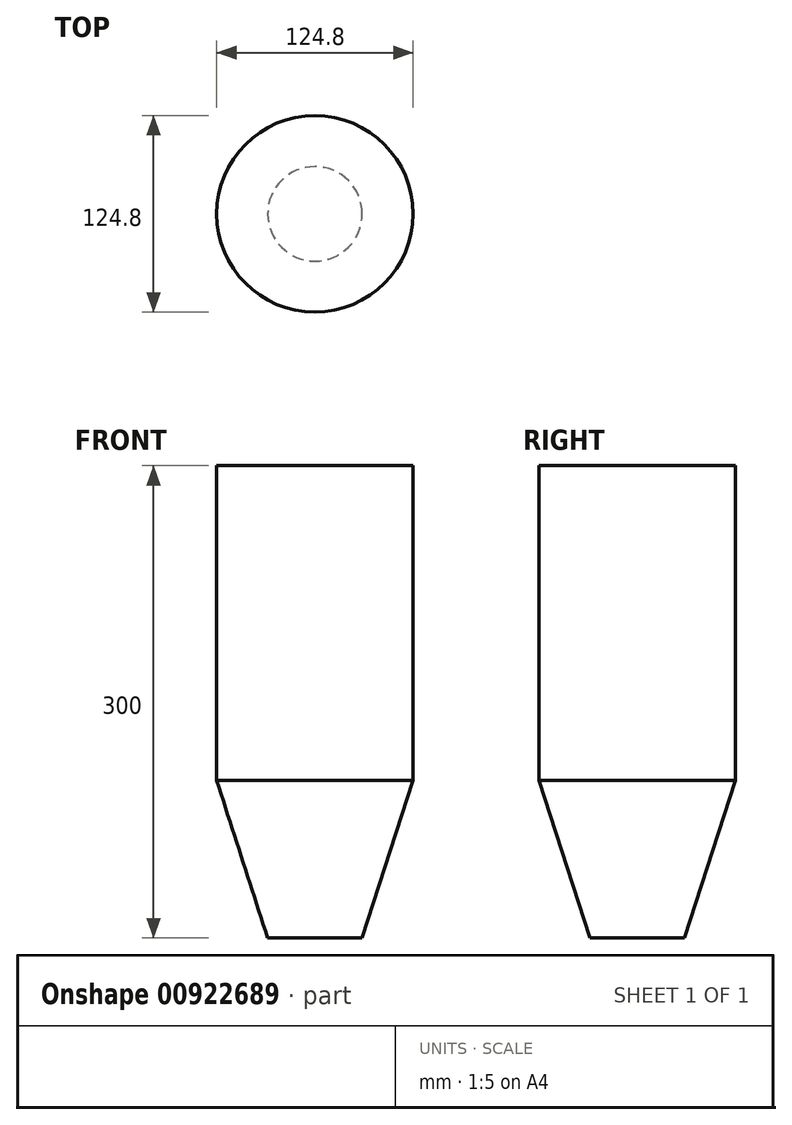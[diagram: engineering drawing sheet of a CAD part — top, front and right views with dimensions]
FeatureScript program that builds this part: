
annotation { "Feature Type Name" : "Feature", "Feature Type Description" : "" }
export const myFeature = defineFeature(function(context is Context, id is Id, definition is map)
    precondition{}
    {
        {
            var Q0;
            Q0=qCreatedBy(makeId("Front.planeOp"),FACE);
            var sketch = newSketch(context, id + "F0", { "sketchPlane" : qUnion([Q0])});
            skLineSegment(sketch, "E0", {"start": v(0, 0) * mm, "end": v(-30, 0) * mm});
            skLineSegment(sketch, "E1", {"start": v(-30, 0) * mm, "end": v(-62.4, 100) * mm});
            skLineSegment(sketch, "E2", {"start": v(-62.4, 100) * mm, "end": v(-62.4, 300) * mm});
            skLineSegment(sketch, "E3", {"start": v(-62.4, 300) * mm, "end": v(0, 300) * mm});
            skLineSegment(sketch, "E4", {"start": v(0, 0) * mm, "end": v(0, 300) * mm});
            skSolve(sketch);
        }
        {
            var Q0;
            Q0=makeQuery(id+"F0.imprint","IMPRINT",FACE,{"disambiguationData":[TD([[makeQuery(id+"F0.imprint","IMPRINT",EDGE,{"derivedFrom":sQuery(id+"F0.wireOp",EDGE,"E0")}),-1.0]])]});
            var Q1;
            Q1=sQuery(id+"F0.wireOp",EDGE,"E4");
            revolve(context, id + "F1", {"surfaceOperationType" : NewSurfaceOperationType.NEW, "entities" : qUnion([Q0]), "axis" : qUnion([Q1]), "revolveType" : RevolveType.FULL});
        }
    });
